# Revit family: СЗ-ВО
name_source: partatom
category: Арматура воздуховодов
units: mm (PartAtom-declared; Revit-internal decimal feet)

## family parameters
Всегда вертикально = Да
На основе рабочей плоскости = Нет
Общий = Нет
При загрузке вырезать с полостями = Нет
Размер круглого соединителя = Использовать диаметр
Тип детали = Присоединяется

## types (11) — shared parameters
00_20_Виробник = Вентс
00_20_Назва = Захисна сітка
URL = https://vents.ua
Висота = 6 мм
Изготовитель = Вентс
Класифікація навантаження = HVAC
Матеріал зони обслуговуваня = <По категории>
Матеріал корпусу = Метал, пофарбований, синій, матовий RAL 5007
Матеріал решітки = Решітка, сталь, пофарбована, RAL5007
zero-valued in all types: Отметка по умолчанию

## per-type parameters (varying)
| type | D1 | D2 | Dy | R1 | d | n | Вага | Діаметр |
| СЗ-ВО-400 | 450 мм | 490 мм | 400 мм | 225 мм | 8 мм | 12 | 1.28 кг | 490 мм |
| СЗ-ВО-450 | 500 мм | 540 мм | 450 мм | 250 мм | 8 мм | 12 | 1.45 кг | 540 мм |
| СЗ-ВО-500 | 560 мм | 600 мм | 500 мм | 280 мм | 12 мм | 12 | 1.77 кг | 600 мм |
| СЗ-ВО-560 | 620 мм | 660 мм | 560 мм | 310 мм | 12 мм | 12 | 2.00 кг | 660 мм |
| СЗ-ВО-630 | 690 мм | 730 мм | 630 мм | 345 мм | 12 мм | 12 | 2.28 кг | 730 мм |
| СЗ-ВО-710 | 770 мм | 810 мм | 710 мм | 385 мм | 12 мм | 16 | 2.28 кг | 810 мм |
| СЗ-ВО-800 | 860 мм | 900 мм | 800 мм | 430 мм | 12 мм | 16 | 2.59 кг | 900 мм |
| СЗ-ВО-900 | 970 мм | 1015 мм | 900 мм | 485 мм | 15 мм | 16 | 3.83 кг | 1015 мм |
| СЗ-ВО-1000 | 1070 мм | 1115 мм | 1000 мм | 535 мм | 15 мм | 16 | 4.32 кг | 1115 мм |
| СЗ-ВО-1120 | 1190 мм | 1270 мм | 1120 мм | 595 мм | 15 мм | 20 | 6.20 кг | 1270 мм |
| СЗ-ВО-1250 | 1320 мм | 1400 мм | 1250 мм | 660 мм | 15 мм | 20 | 7.03 кг | 1400 мм |

note: column(s) folded — value = type name in every type: 00_20_Тип
